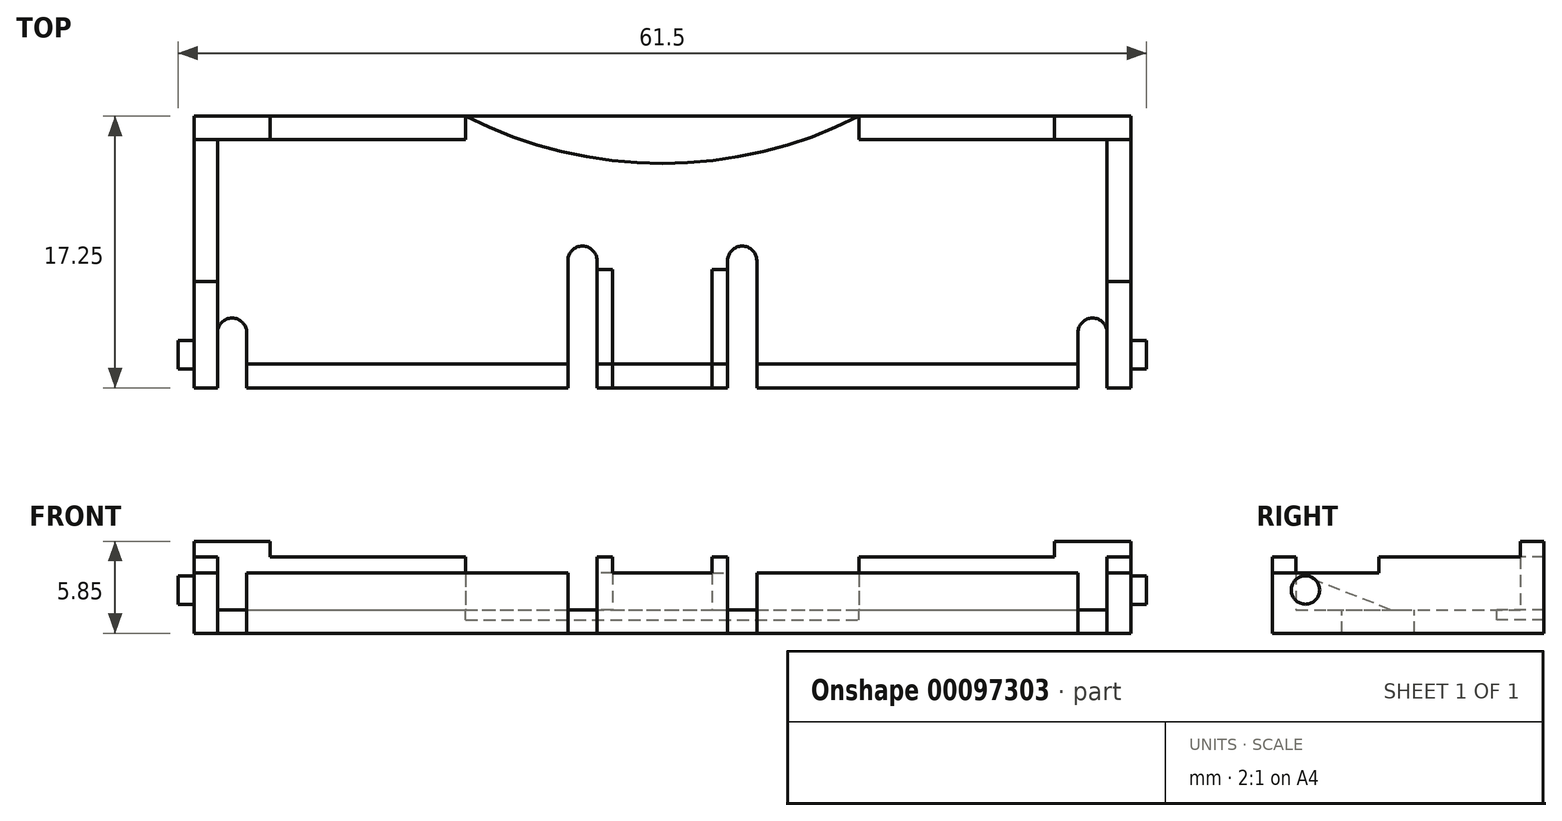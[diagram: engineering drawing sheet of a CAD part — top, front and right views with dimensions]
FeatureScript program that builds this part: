
annotation { "Feature Type Name" : "Feature", "Feature Type Description" : "" }
export const myFeature = defineFeature(function(context is Context, id is Id, definition is map)
    precondition{}
    {
        {
            var Q0;
            Q0=qCreatedBy(makeId("Top.planeOp"),FACE);
            var sketch = newSketch(context, id + "F0", { "sketchPlane" : qUnion([Q0])});
            skLineSegment(sketch, "E0.bottom", {"start": v(-59.5, 0) * mm, "end": v(0, 0) * mm});
            skLineSegment(sketch, "E0.top", {"start": v(-59.5, 17.25) * mm, "end": v(0, 17.25) * mm});
            skLineSegment(sketch, "E0.left", {"start": v(-59.5, 0) * mm, "end": v(-59.5, 17.25) * mm});
            skLineSegment(sketch, "E0.right", {"start": v(0, 0) * mm, "end": v(0, 17.25) * mm});
            skSolve(sketch);
        }
        {
            var Q0;
            Q0=makeQuery(id+"F0.imprint","IMPRINT",FACE,{"disambiguationData":[TD([[makeQuery(id+"F0.imprint","IMPRINT",EDGE,{"derivedFrom":sQuery(id+"F0.wireOp",EDGE,"E0.bottom")}),1.0]])]});
            extrude(context, id + "F1", {"entities" : qUnion([Q0]), "depth" : 4.85 * mm});
        }
        {
            var Q0;
            Q0=makeQuery(id+"F1.opExtrude","CAP_FACE",FACE,{"disambiguationData":[OSD([sQuery(id+"F0.wireOp",EDGE,"E0.bottom"),sQuery(id+"F0.wireOp",EDGE,"E0.top"),sQuery(id+"F0.wireOp",EDGE,"E0.left"),sQuery(id+"F0.wireOp",EDGE,"E0.right")])],"isStart":false});
            shell(context, id + "F2", {"entities" : qUnion([Q0]), "thickness" : 1.5 * mm});
        }
        {
            var Q0;
            Q0=makeQuery(id+"F1.opExtrude","CAP_FACE",FACE,{"disambiguationData":[OSD([sQuery(id+"F0.wireOp",EDGE,"E0.bottom"),sQuery(id+"F0.wireOp",EDGE,"E0.top"),sQuery(id+"F0.wireOp",EDGE,"E0.left"),sQuery(id+"F0.wireOp",EDGE,"E0.right")])],"isStart":false});
            var sketch = newSketch(context, id + "F3", { "sketchPlane" : qUnion([Q0])});
            skLineSegment(sketch, "E1", {"start": v(-56.15, 0) * mm, "end": v(-56.15, 3.5) * mm});
            skLineSegment(sketch, "E2", {"start": v(-58, 0) * mm, "end": v(-58, 3.5) * mm});
            skLineSegment(sketch, "E3", {"start": v(-58, 0) * mm, "end": v(-56.15, 0) * mm});
            skArc(sketch, "E4", {"start": v(-56.15, 3.5) * mm, "mid": v(-57.08, 4.43) * mm, "end": v(-58, 3.5) * mm});
            skLineSegment(sketch, "E5", {"start": v(-35.75, 0) * mm, "end": v(-35.75, 8.08) * mm});
            skLineSegment(sketch, "E6", {"start": v(-35.75, 0) * mm, "end": v(-33.9, 0) * mm});
            skLineSegment(sketch, "E7", {"start": v(-33.9, 0) * mm, "end": v(-33.9, 8.08) * mm});
            skArc(sketch, "E8", {"start": v(-33.9, 8.08) * mm, "mid": v(-34.83, 9) * mm, "end": v(-35.75, 8.08) * mm});
            skLineSegment(sketch, "E9", {"start": v(-1.5, 0) * mm, "end": v(-1.5, 3.5) * mm});
            skLineSegment(sketch, "E10", {"start": v(-1.5, 0) * mm, "end": v(-3.35, 0) * mm});
            skLineSegment(sketch, "E11", {"start": v(-3.35, 0) * mm, "end": v(-3.35, 3.5) * mm});
            skLineSegment(sketch, "E12", {"start": v(-23.75, 0) * mm, "end": v(-23.75, 8.08) * mm});
            skLineSegment(sketch, "E13", {"start": v(-23.75, 0) * mm, "end": v(-25.6, 0) * mm});
            skLineSegment(sketch, "E14", {"start": v(-25.6, 0) * mm, "end": v(-25.6, 8.08) * mm});
            skArc(sketch, "E15", {"start": v(-23.75, 8.08) * mm, "mid": v(-24.68, 9) * mm, "end": v(-25.6, 8.08) * mm});
            skArc(sketch, "E16", {"start": v(-1.5, 3.5) * mm, "mid": v(-2.43, 4.42) * mm, "end": v(-3.35, 3.5) * mm});
            skSolve(sketch);
        }
        {
            var Q0;
            {var subQ0=sQuery(id+"F3.wireOp",EDGE,"E8");Q0=makeQuery(id+"F3.imprint","IMPRINT",FACE,{"disambiguationData":[TD([[makeQuery(id+"F3.imprint","IMPRINT",EDGE,{"derivedFrom":subQ0}),1.0]])]});}
            var Q1;
            {var subQ0=sQuery(id+"F3.wireOp",EDGE,"E6");Q1=makeQuery(id+"F3.imprint","IMPRINT",FACE,{"disambiguationData":[TD([[makeQuery(id+"F3.imprint","IMPRINT",EDGE,{"derivedFrom":subQ0}),1.0]])]});}
            var Q2;
            {var subQ0=sQuery(id+"F3.wireOp",EDGE,"E4");Q2=makeQuery(id+"F3.imprint","IMPRINT",FACE,{"disambiguationData":[TD([[makeQuery(id+"F3.imprint","IMPRINT",EDGE,{"derivedFrom":subQ0}),1.0]])]});}
            var Q3;
            {var subQ0=sQuery(id+"F3.wireOp",EDGE,"E3");Q3=makeQuery(id+"F3.imprint","IMPRINT",FACE,{"disambiguationData":[TD([[makeQuery(id+"F3.imprint","IMPRINT",EDGE,{"derivedFrom":subQ0}),1.0]])]});}
            var Q4;
            {var subQ0=sQuery(id+"F3.wireOp",EDGE,"E15");Q4=makeQuery(id+"F3.imprint","IMPRINT",FACE,{"disambiguationData":[TD([[makeQuery(id+"F3.imprint","IMPRINT",EDGE,{"derivedFrom":subQ0}),1.0]])]});}
            var Q5;
            {var subQ0=sQuery(id+"F3.wireOp",EDGE,"E13");Q5=makeQuery(id+"F3.imprint","IMPRINT",FACE,{"disambiguationData":[TD([[makeQuery(id+"F3.imprint","IMPRINT",EDGE,{"derivedFrom":subQ0}),1.0]])]});}
            var Q6;
            {var subQ4=sQuery(id+"F3.wireOp",EDGE,"E16");Q6=makeQuery(id+"F3.imprint","IMPRINT",FACE,{"disambiguationData":[TD([[makeQuery(id+"F3.imprint","IMPRINT",EDGE,{"derivedFrom":subQ4}),1.0]])]});}
            var Q7;
            {var subQ5=sQuery(id+"F3.wireOp",EDGE,"E10");Q7=makeQuery(id+"F3.imprint","IMPRINT",FACE,{"disambiguationData":[TD([[makeQuery(id+"F3.imprint","IMPRINT",EDGE,{"derivedFrom":subQ5}),1.0]])]});}
            extrude(context, id + "F4", {"entities" : qUnion([Q0, Q1, Q2, Q3, Q4, Q5, Q6, Q7]), "operationType" : NewBodyOperationType.REMOVE, "endBound" : BoundingType.THROUGH_ALL, "oppositeDirection" : true, "depth" : 25 * mm});
        }
        {
            var Q0;
            {var subQ0=sQuery(id+"F0.wireOp",EDGE,"E0.right");var subQ1=sQuery(id+"F0.wireOp",EDGE,"E0.top");var subQ2=sQuery(id+"F0.wireOp",EDGE,"E0.left");var subQ3=sQuery(id+"F0.wireOp",EDGE,"E0.bottom");Q0=makeQuery(id+"F4.boolean.opBoolean","SPLIT",FACE,{"disambiguationData":[TD([makeQuery(id+"F1.opExtrude","SWEPT_FACE",FACE,{"disambiguationData":[OSD([subQ1])]})])],"derivedFrom":makeQuery(id+"F1.opExtrude","CAP_FACE",FACE,{"disambiguationData":[OSD([subQ3,subQ1,subQ2,subQ0])],"isStart":false})});}
            var sketch = newSketch(context, id + "F5", { "sketchPlane" : qUnion([Q0])});
            skArc(sketch, "E17", {"start": v(-42.25, 17.25) * mm, "mid": v(-29.75, 14.25) * mm, "end": v(-17.25, 17.25) * mm});
            skLineSegment(sketch, "E18.0", {"start": v(-42.25, 17.25) * mm, "end": v(-17.25, 17.25) * mm});
            skPoint(sketch, "E19.orphan", {"position": v(0, 17.25) * mm});
            skPoint(sketch, "E20.orphan", {"position": v(-59.5, 17.25) * mm});
            skSolve(sketch);
        }
        {
            var Q0;
            {var subQ0=sQuery(id+"F5.wireOp",EDGE,"E17");var subQ1=sQuery(id+"F0.wireOp",EDGE,"E0.top");var subQ2=makeQuery(id+"F2.opShell","OFFSET_EDGE",EDGE,{"disambiguationData":[OSD([subQ1]),TDD([makeQuery(id+"F1.opExtrude","CAP_EDGE",EDGE,{"disambiguationData":[OSD([subQ1])],"isStart":false})])]});var subQ3=makeQuery(id+"F5.imprint","INTERSECT",VERTEX,{"disambiguationData":[OD(0.0)],"derivedFrom":[subQ2,subQ0]});Q0=makeQuery(id+"F5.imprint","IMPRINT",FACE,{"disambiguationData":[TD([[makeQuery(id+"F5.imprint","IMPRINT",EDGE,{"disambiguationData":[TD([[subQ3,-1.0]])],"derivedFrom":subQ0}),1.0]])]});}
            var Q1;
            {var subQ0=sQuery(id+"F5.wireOp",EDGE,"E18.0");Q1=makeQuery(id+"F5.imprint","IMPRINT",FACE,{"disambiguationData":[TD([[makeQuery(id+"F5.imprint","IMPRINT",EDGE,{"derivedFrom":subQ0}),-1.0]])]});}
            extrude(context, id + "F6", {"entities" : qUnion([Q0, Q1]), "operationType" : NewBodyOperationType.REMOVE, "oppositeDirection" : true, "depth" : 4 * mm});
        }
        {
            var Q0;
            Q0=makeQuery(id+"F2.opShell","OFFSET_FACE",FACE,{"disambiguationData":[OSD([sQuery(id+"F0.wireOp",EDGE,"E0.bottom"),sQuery(id+"F0.wireOp",EDGE,"E0.top"),sQuery(id+"F0.wireOp",EDGE,"E0.left"),sQuery(id+"F0.wireOp",EDGE,"E0.right")])]});
            var sketch = newSketch(context, id + "F7", { "sketchPlane" : qUnion([Q0])});
            skLineSegment(sketch, "E21.0", {"start": v(-42.25, 15.75) * mm, "end": v(-38.72, 15.75) * mm});
            skArc(sketch, "E22.0", {"start": v(-42.25, 17.25) * mm, "mid": v(-40.5, 16.44) * mm, "end": v(-38.72, 15.75) * mm});
            skLineSegment(sketch, "E23.0", {"start": v(-20.78, 15.75) * mm, "end": v(-17.25, 15.75) * mm});
            skArc(sketch, "E24.0", {"start": v(-20.78, 15.75) * mm, "mid": v(-19, 16.44) * mm, "end": v(-17.25, 17.25) * mm});
            skLineSegment(sketch, "E25", {"start": v(-17.25, 17.25) * mm, "end": v(-17.25, 15.75) * mm});
            skLineSegment(sketch, "E26", {"start": v(-42.25, 17.25) * mm, "end": v(-42.25, 15.75) * mm});
            skPoint(sketch, "E27.orphan", {"position": v(-1.5, 15.75) * mm});
            skPoint(sketch, "E28.orphan", {"position": v(-58, 15.75) * mm});
            skSolve(sketch);
        }
        {
            var Q0;
            Q0 = qSketchRegion(id + "F7", true);
            extrude(context, id + "F8", {"entities" : qUnion([Q0]), "operationType" : NewBodyOperationType.REMOVE, "endBound" : BoundingType.THROUGH_ALL, "depth" : 4.18 * mm});
        }
        {
            var Q0;
            {var subQ0=sQuery(id+"F0.wireOp",EDGE,"E0.top");var subQ2=sQuery(id+"F0.wireOp",EDGE,"E0.left");var subQ3=makeQuery(id+"F1.opExtrude","SWEPT_FACE",FACE,{"disambiguationData":[OSD([subQ2])]});var subQ5=makeQuery(id+"F1.opExtrude","SWEPT_FACE",FACE,{"disambiguationData":[OSD([subQ0])]});var subQ6=sQuery(id+"F0.wireOp",EDGE,"E0.bottom");var subQ9=sQuery(id+"F0.wireOp",EDGE,"E0.right");Q0=makeQuery(id+"F6.boolean.opBoolean","SPLIT",FACE,{"disambiguationData":[TD([subQ3])],"derivedFrom":makeQuery(id+"F4.boolean.opBoolean","SPLIT",FACE,{"disambiguationData":[TD([subQ5])],"derivedFrom":makeQuery(id+"F1.opExtrude","CAP_FACE",FACE,{"disambiguationData":[OSD([subQ6,subQ0,subQ2,subQ9])],"isStart":false})})});}
            var sketch = newSketch(context, id + "F9", { "sketchPlane" : qUnion([Q0])});
            skLineSegment(sketch, "E29.bottom", {"start": v(-60.55, 6.75) * mm, "end": v(1.72, 6.75) * mm});
            skLineSegment(sketch, "E29.top", {"start": v(-60.55, -8.74) * mm, "end": v(1.72, -8.74) * mm});
            skLineSegment(sketch, "E29.left", {"start": v(-60.55, 6.75) * mm, "end": v(-60.55, -8.74) * mm});
            skLineSegment(sketch, "E29.right", {"start": v(1.72, 6.75) * mm, "end": v(1.72, -8.74) * mm});
            skSolve(sketch);
        }
        {
            var Q0;
            {var subQ0=sQuery(id+"F9.wireOp",EDGE,"E29.bottom");var subQ1=sQuery(id+"F0.wireOp",EDGE,"E0.left");var subQ2=makeQuery(id+"F1.opExtrude","CAP_EDGE",EDGE,{"disambiguationData":[OSD([subQ1])],"isStart":false});var subQ3=makeQuery(id+"F9.imprint","INTERSECT",VERTEX,{"derivedFrom":[subQ2,subQ0]});Q0=makeQuery(id+"F9.imprint","IMPRINT",FACE,{"disambiguationData":[TD([[makeQuery(id+"F9.imprint","IMPRINT",EDGE,{"disambiguationData":[TD([[subQ3,-1.0]])],"derivedFrom":subQ0}),-1.0]])]});}
            var Q1;
            Q1=makeQuery(id+"F9.imprint","IMPRINT",FACE,{"disambiguationData":[TD([[makeQuery(id+"F9.imprint","IMPRINT",EDGE,{"derivedFrom":sQuery(id+"F9.wireOp",EDGE,"E29.top")}),1.0]])]});
            extrude(context, id + "F10", {"entities" : qUnion([Q0, Q1]), "operationType" : NewBodyOperationType.REMOVE, "oppositeDirection" : true, "depth" : 1 * mm});
        }
        {
            var Q0;
            {var subQ0=sQuery(id+"F0.wireOp",EDGE,"E0.top");var subQ2=sQuery(id+"F0.wireOp",EDGE,"E0.left");var subQ3=makeQuery(id+"F1.opExtrude","SWEPT_FACE",FACE,{"disambiguationData":[OSD([subQ2])]});var subQ5=makeQuery(id+"F1.opExtrude","SWEPT_FACE",FACE,{"disambiguationData":[OSD([subQ0])]});var subQ6=sQuery(id+"F0.wireOp",EDGE,"E0.bottom");var subQ9=sQuery(id+"F0.wireOp",EDGE,"E0.right");Q0=makeQuery(id+"F6.boolean.opBoolean","SPLIT",FACE,{"disambiguationData":[TD([subQ3])],"derivedFrom":makeQuery(id+"F4.boolean.opBoolean","SPLIT",FACE,{"disambiguationData":[TD([subQ5])],"derivedFrom":makeQuery(id+"F1.opExtrude","CAP_FACE",FACE,{"disambiguationData":[OSD([subQ6,subQ0,subQ2,subQ9])],"isStart":false})})});}
            var sketch = newSketch(context, id + "F11", { "sketchPlane" : qUnion([Q0])});
            skLineSegment(sketch, "E30.bottom", {"start": v(-59.5, 17.25) * mm, "end": v(-54.65, 17.25) * mm});
            skLineSegment(sketch, "E30.top", {"start": v(-59.5, 15.75) * mm, "end": v(-54.65, 15.75) * mm});
            skLineSegment(sketch, "E30.left", {"start": v(-59.5, 17.25) * mm, "end": v(-59.5, 15.75) * mm});
            skLineSegment(sketch, "E30.right", {"start": v(-54.65, 17.25) * mm, "end": v(-54.65, 15.75) * mm});
            skLineSegment(sketch, "E31.bottom", {"start": v(-4.85, 17.25) * mm, "end": v(0, 17.25) * mm});
            skLineSegment(sketch, "E31.top", {"start": v(-4.85, 15.75) * mm, "end": v(0, 15.75) * mm});
            skLineSegment(sketch, "E31.left", {"start": v(-4.85, 17.25) * mm, "end": v(-4.85, 15.75) * mm});
            skLineSegment(sketch, "E31.right", {"start": v(0, 17.25) * mm, "end": v(0, 15.75) * mm});
            skSolve(sketch);
        }
        {
            var Q0;
            Q0=makeQuery(id+"F11.imprint","IMPRINT",FACE,{"disambiguationData":[TD([[makeQuery(id+"F11.imprint","IMPRINT",EDGE,{"derivedFrom":sQuery(id+"F11.wireOp",EDGE,"E30.bottom")}),-1.0]])]});
            var Q1;
            Q1=makeQuery(id+"F11.imprint","IMPRINT",FACE,{"disambiguationData":[TD([[makeQuery(id+"F11.imprint","IMPRINT",EDGE,{"derivedFrom":sQuery(id+"F11.wireOp",EDGE,"E31.bottom")}),-1.0]])]});
            extrude(context, id + "F12", {"entities" : qUnion([Q0, Q1]), "operationType" : NewBodyOperationType.ADD, "depth" : 1 * mm});
        }
        {
            var Q0;
            Q0=makeQuery(id+"F4.boolean.opBoolean","COPY",FACE,{"derivedFrom":makeQuery(id+"F4.opExtrude","SWEPT_FACE",FACE,{"disambiguationData":[OSD([sQuery(id+"F3.wireOp",EDGE,"E7")])]})});
            var sketch = newSketch(context, id + "F13", { "sketchPlane" : qUnion([Q0])});
            skLineSegment(sketch, "E32", {"start": v(0, 4.85) * mm, "end": v(0, 1.5) * mm});
            skLineSegment(sketch, "E33", {"start": v(-7.5, 1.5) * mm, "end": v(0, 1.5) * mm});
            skLineSegment(sketch, "E34", {"start": v(0, 4.85) * mm, "end": v(-1.5, 4.85) * mm});
            skLineSegment(sketch, "E35", {"start": v(-1.5, 4.85) * mm, "end": v(-1.5, 3.85) * mm});
            skLineSegment(sketch, "E36", {"start": v(-7.5, 1.5) * mm, "end": v(-1.5, 3.85) * mm});
            skSolve(sketch);
        }
        {
            var Q0;
            {var subQ4=sQuery(id+"F13.wireOp",EDGE,"E36");Q0=makeQuery(id+"F13.imprint","IMPRINT",FACE,{"disambiguationData":[TD([[makeQuery(id+"F13.imprint","IMPRINT",EDGE,{"derivedFrom":subQ4}),-1.0]])]});}
            var Q1;
            {var subQ2=sQuery(id+"F13.wireOp",EDGE,"E34");Q1=makeQuery(id+"F13.imprint","IMPRINT",FACE,{"disambiguationData":[TD([[makeQuery(id+"F13.imprint","IMPRINT",EDGE,{"derivedFrom":subQ2}),1.0]])]});}
            var Q2;
            Q2=makeQuery(id+"F4.boolean.opBoolean","COPY",FACE,{"derivedFrom":makeQuery(id+"F4.opExtrude","SWEPT_FACE",FACE,{"disambiguationData":[OSD([sQuery(id+"F3.wireOp",EDGE,"E14")])]})});
            extrude(context, id + "F14", {"entities" : qUnion([Q0, Q1]), "operationType" : NewBodyOperationType.ADD, "oppositeDirection" : true, "endBoundEntityFace" : qUnion([Q2]), "depth" : 1 * mm});
        }
        {
            var Q0;
            Q0=makeQuery(id+"F4.boolean.opBoolean","COPY",FACE,{"derivedFrom":makeQuery(id+"F4.opExtrude","SWEPT_FACE",FACE,{"disambiguationData":[OSD([sQuery(id+"F3.wireOp",EDGE,"E14")])]})});
            var sketch = newSketch(context, id + "F15", { "sketchPlane" : qUnion([Q0])});
            skLineSegment(sketch, "E37.0", {"start": v(0, 4.85) * mm, "end": v(0, 3.85) * mm});
            skLineSegment(sketch, "E38.0", {"start": v(0, 4.85) * mm, "end": v(1.5, 4.85) * mm});
            skLineSegment(sketch, "E39.0", {"start": v(1.5, 4.85) * mm, "end": v(1.5, 3.85) * mm});
            skLineSegment(sketch, "E40.0", {"start": v(7.5, 1.5) * mm, "end": v(1.5, 3.85) * mm});
            skLineSegment(sketch, "E41.0", {"start": v(1.5, 3.85) * mm, "end": v(1.5, 1.5) * mm});
            skLineSegment(sketch, "E42.0", {"start": v(1.5, 1.5) * mm, "end": v(7.5, 1.5) * mm});
            skSolve(sketch);
        }
        {
            var Q0;
            Q0=makeQuery(id+"F15.imprint","IMPRINT",FACE,{"disambiguationData":[TD([[makeQuery(id+"F15.imprint","IMPRINT",EDGE,{"derivedFrom":sQuery(id+"F15.wireOp",EDGE,"E37.0")}),1.0]])]});
            var Q1;
            Q1=makeQuery(id+"F15.imprint","IMPRINT",FACE,{"disambiguationData":[TD([[makeQuery(id+"F15.imprint","IMPRINT",EDGE,{"derivedFrom":sQuery(id+"F15.wireOp",EDGE,"E40.0")}),1.0]])]});
            extrude(context, id + "F16", {"entities" : qUnion([Q0, Q1]), "operationType" : NewBodyOperationType.ADD, "oppositeDirection" : true, "depth" : 1 * mm});
        }
        {
            var Q0;
            Q0=makeQuery(id+"F12.boolean.opBoolean","MERGE",FACE,{"derivedFrom":[makeQuery(id+"F1.opExtrude","SWEPT_FACE",FACE,{"disambiguationData":[OSD([sQuery(id+"F0.wireOp",EDGE,"E0.right")])]}),makeQuery(id+"F12.opExtrude","SWEPT_FACE",FACE,{"disambiguationData":[OSD([sQuery(id+"F11.wireOp",EDGE,"E31.right")])]})]});
            var sketch = newSketch(context, id + "F17", { "sketchPlane" : qUnion([Q0])});
            skCircle(sketch, "E43", {"center": v(2.1, 2.75) * mm, "radius": 0.9 * mm});
            skSolve(sketch);
        }
        {
            var Q0;
            Q0=makeQuery(id+"F17.imprint","IMPRINT",FACE,{"disambiguationData":[TD([[makeQuery(id+"F17.imprint","IMPRINT",EDGE,{"derivedFrom":sQuery(id+"F17.wireOp",EDGE,"E43")}),1.0]])]});
            extrude(context, id + "F18", {"entities" : qUnion([Q0]), "operationType" : NewBodyOperationType.ADD, "depth" : 1 * mm});
        }
        {
            var Q0;
            Q0=makeQuery(id+"F12.boolean.opBoolean","MERGE",FACE,{"derivedFrom":[makeQuery(id+"F1.opExtrude","SWEPT_FACE",FACE,{"disambiguationData":[OSD([sQuery(id+"F0.wireOp",EDGE,"E0.left")])]}),makeQuery(id+"F12.opExtrude","SWEPT_FACE",FACE,{"disambiguationData":[OSD([sQuery(id+"F11.wireOp",EDGE,"E30.left")])]})]});
            var sketch = newSketch(context, id + "F19", { "sketchPlane" : qUnion([Q0])});
            skCircle(sketch, "E44", {"center": v(-2.1, 2.75) * mm, "radius": 0.9 * mm});
            skSolve(sketch);
        }
        {
            var Q0;
            Q0=makeQuery(id+"F19.imprint","IMPRINT",FACE,{"disambiguationData":[TD([[makeQuery(id+"F19.imprint","IMPRINT",EDGE,{"derivedFrom":sQuery(id+"F19.wireOp",EDGE,"E44")}),1.0]])]});
            extrude(context, id + "F20", {"entities" : qUnion([Q0]), "operationType" : NewBodyOperationType.ADD, "depth" : 1 * mm});
        }
    });
